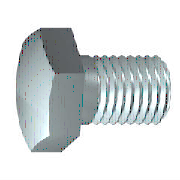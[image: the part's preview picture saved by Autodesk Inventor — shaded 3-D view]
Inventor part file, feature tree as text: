
AUTODESK INVENTOR PART (.ipt)
format: ipt  version: 2023.1 (Build 271208000, 208)  size: 209,408 bytes
history: native  units: mm (DEFAULTED — no unit token found)
features: sketch x4, other x3, revolve x2, extrude x2, fillet x1
ambient origin geometry x8: Origin, YZ Plane, XZ Plane, XY Plane, X Axis, Y Axis, Z Axis, Center Point
bodies: Solid1 (feature_tree)
feature tree (12):
  revolve  "Revolution1"  Angle=45.0deg
  extrude  "Extrusion1"  TaperAngle=60.0deg  [1 undecoded]
  revolve  "Revolution2"  Angle=30.0deg
  extrude  "Extrusion2"  TaperAngle=0.0deg  [1 undecoded]
  other  "MSC_A1"
  other  "MSC_PF1"
  other  "MSC_PT1"
  fillet  "Fillet1"  [1 undecoded]
  sketch  "Sketch2"  dims[d3=30.0deg d5=45.0deg]
  sketch  "Sketch3"  dims[d8=90.0deg d9=60.0deg]
  sketch  "Sketch4"  dims[d13=0.0mm d14=30.0deg]
  sketch  "Sketch5"  dims[d16=90.0deg d18=0.0mm d22=0.0mm d23=0.0mm d25=0.0mm d26=0.0mm d27=18.0mm d28=2.0mm d29=0.0mm d30=0.6mm d31=0.0mm]
note: 3 required parameter values undecoded (feature->parameter linkage not recoverable at this tier; creation-order binding heuristic only, values carry confidence <= 0.55)
